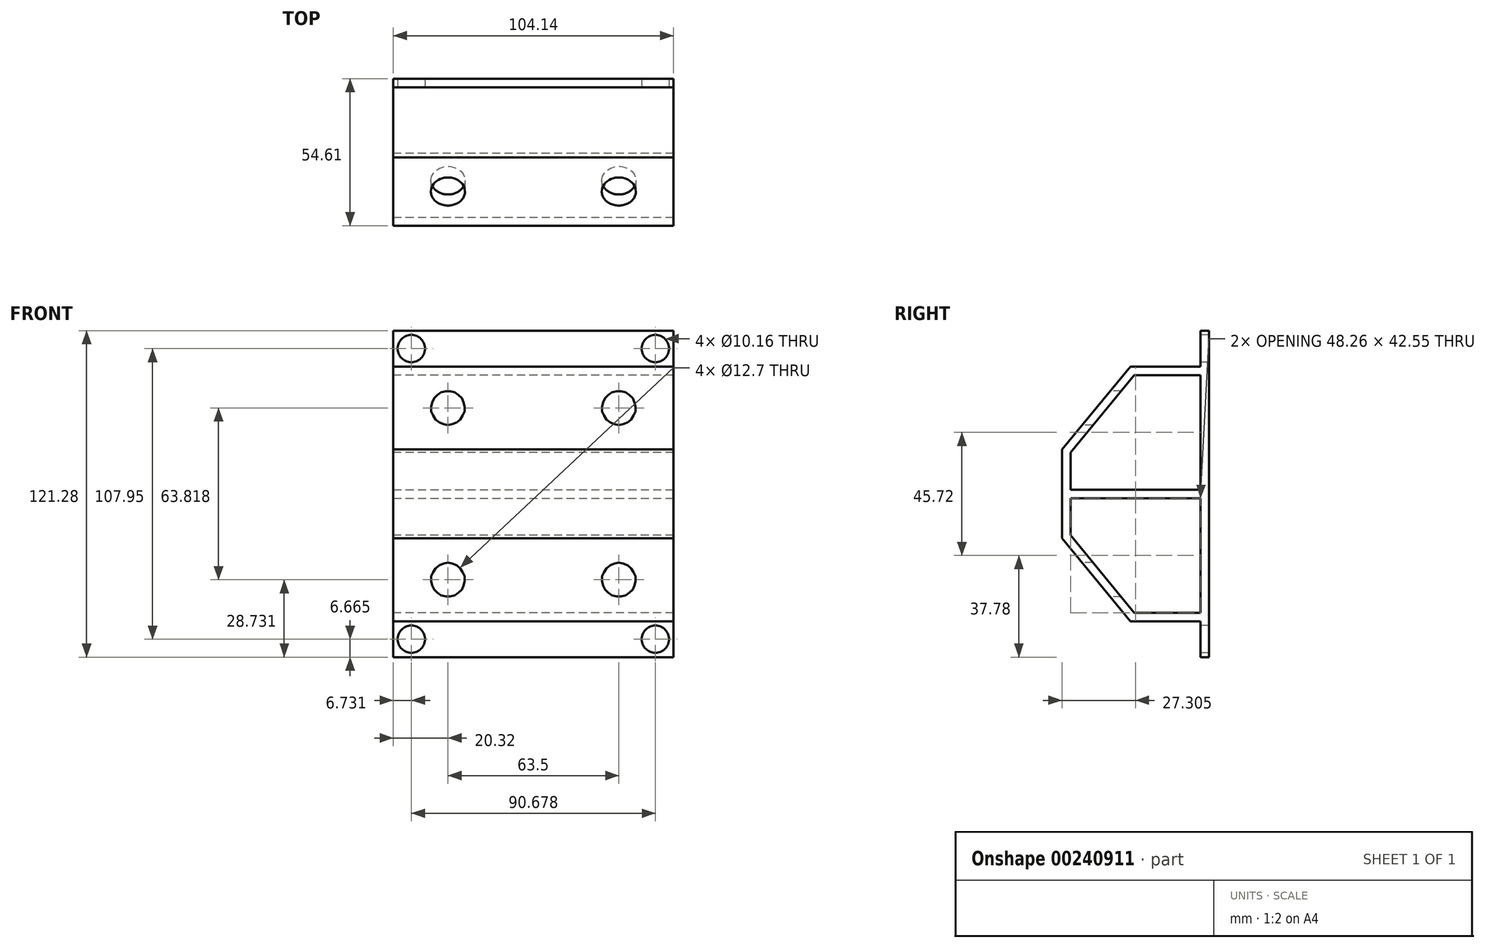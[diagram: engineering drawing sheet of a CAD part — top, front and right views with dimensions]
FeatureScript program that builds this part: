
annotation { "Feature Type Name" : "Feature", "Feature Type Description" : "" }
export const myFeature = defineFeature(function(context is Context, id is Id, definition is map)
    precondition{}
    {
        {
            var Q0;
            Q0=qCreatedBy(makeId("Right.planeOp"),FACE);
            var sketch = newSketch(context, id + "F0", { "sketchPlane" : qUnion([Q0])});
            skLineSegment(sketch, "E0", {"start": v(0, 0) * mm, "end": v(57.67, 0) * mm, "construction": true});
            skLineSegment(sketch, "E1", {"start": v(29.21, 47.3) * mm, "end": v(0, 47.3) * mm});
            skLineSegment(sketch, "E2", {"start": v(0, 47.3) * mm, "end": v(-25.4, 16.51) * mm});
            skLineSegment(sketch, "E3", {"start": v(-25.4, 16.51) * mm, "end": v(-25.4, 0) * mm});
            skLineSegment(sketch, "E4", {"start": v(0, 0) * mm, "end": v(0, 100.35) * mm, "construction": true});
            skLineSegment(sketch, "E5", {"start": v(29.21, 47.3) * mm, "end": v(29.21, 0) * mm});
            skLineSegment(sketch, "E6.MirrorCS", {"start": v(29.21, -47.3) * mm, "end": v(29.21, 0) * mm});
            skLineSegment(sketch, "E7.MirrorCS", {"start": v(0, -47.3) * mm, "end": v(-25.4, -16.51) * mm});
            skLineSegment(sketch, "E8.MirrorCS", {"start": v(-25.4, -16.51) * mm, "end": v(-25.4, 0) * mm});
            skLineSegment(sketch, "E9.MirrorCS", {"start": v(29.21, -47.3) * mm, "end": v(0, -47.3) * mm});
            skLineSegment(sketch, "E10", {"start": v(-22.22, 3.17) * mm, "end": v(26.04, 3.17) * mm});
            skLineSegment(sketch, "E11.MirrorCS", {"start": v(-22.22, -3.17) * mm, "end": v(26.04, -3.17) * mm});
            skLineSegment(sketch, "E12.0", {"start": v(26.04, 44.13) * mm, "end": v(1.5, 44.13) * mm});
            skLineSegment(sketch, "E12.1", {"start": v(26.03, 44.13) * mm, "end": v(26.04, 0) * mm});
            skLineSegment(sketch, "E12.2", {"start": v(1.5, 44.13) * mm, "end": v(-22.22, 15.37) * mm});
            skLineSegment(sketch, "E12.3", {"start": v(26.04, -44.13) * mm, "end": v(26.03, 0) * mm});
            skLineSegment(sketch, "E12.4", {"start": v(-22.22, 15.37) * mm, "end": v(-22.22, 0) * mm});
            skLineSegment(sketch, "E12.5", {"start": v(-22.22, -15.37) * mm, "end": v(-22.22, 0) * mm});
            skLineSegment(sketch, "E12.6", {"start": v(1.5, -44.13) * mm, "end": v(-22.23, -15.37) * mm});
            skLineSegment(sketch, "E12.7", {"start": v(26.04, -44.13) * mm, "end": v(1.5, -44.13) * mm});
            skPoint(sketch, "E13.orphan", {"position": v(-25.4, 3.17) * mm});
            skPoint(sketch, "E14.orphan", {"position": v(-25.4, -3.17) * mm});
            skPoint(sketch, "E15.orphan", {"position": v(29.21, 3.18) * mm});
            skPoint(sketch, "E16.orphan", {"position": v(29.21, -3.18) * mm});
            skLineSegment(sketch, "E17", {"start": v(-22.22, 3.17) * mm, "end": v(-22.22, -3.17) * mm});
            skLineSegment(sketch, "E18", {"start": v(26.04, 3.18) * mm, "end": v(26.04, -3.18) * mm});
            skSolve(sketch);
        }
        {
            var Q0;
            Q0=qSketchRegion(id+"F0",true);
            extrude(context, id + "F1", {"entities" : qUnion([Q0]), "depth" : 52.07 * mm, "hasSecondDirection" : true, "secondDirectionOppositeDirection" : true, "secondDirectionDepth" : 52.07 * mm});
        }
        {
            var Q0;
            Q0=makeQuery(id+"F1.opExtrude","CAP_FACE",FACE,{"disambiguationData":[OSD([sQuery(id+"F0.wireOp",EDGE,"E1"),sQuery(id+"F0.wireOp",EDGE,"E2"),sQuery(id+"F0.wireOp",EDGE,"E3"),sQuery(id+"F0.wireOp",EDGE,"E5"),sQuery(id+"F0.wireOp",EDGE,"E6.MirrorCS"),sQuery(id+"F0.wireOp",EDGE,"E7.MirrorCS"),sQuery(id+"F0.wireOp",EDGE,"E8.MirrorCS"),sQuery(id+"F0.wireOp",EDGE,"E9.MirrorCS"),sQuery(id+"F0.wireOp",EDGE,"E12.0"),sQuery(id+"F0.wireOp",EDGE,"E12.1"),sQuery(id+"F0.wireOp",EDGE,"E12.2"),sQuery(id+"F0.wireOp",EDGE,"E12.3"),sQuery(id+"F0.wireOp",EDGE,"E12.4"),sQuery(id+"F0.wireOp",EDGE,"E12.5"),sQuery(id+"F0.wireOp",EDGE,"E12.6"),sQuery(id+"F0.wireOp",EDGE,"E12.7"),sQuery(id+"F0.wireOp",EDGE,"E17"),sQuery(id+"F0.wireOp",EDGE,"E18")])],"isStart":false});
            var sketch = newSketch(context, id + "F2", { "sketchPlane" : qUnion([Q0])});
            skLineSegment(sketch, "E19", {"start": v(-22.22, 1.59) * mm, "end": v(26.04, 1.59) * mm});
            skLineSegment(sketch, "E20", {"start": v(0, 0) * mm, "end": v(9.33, 0) * mm, "construction": true});
            skLineSegment(sketch, "E21.MirrorCS", {"start": v(-22.22, -1.59) * mm, "end": v(26.04, -1.59) * mm});
            skLineSegment(sketch, "E22", {"start": v(-22.22, 1.59) * mm, "end": v(-22.22, -1.59) * mm});
            skLineSegment(sketch, "E23", {"start": v(26.04, 1.59) * mm, "end": v(26.04, -1.59) * mm});
            skSolve(sketch);
        }
        {
            var Q0;
            Q0=qSketchRegion(id+"F2",true);
            var Q1;
            Q1=makeQuery(id+"F1.opExtrude","CAP_FACE",FACE,{"disambiguationData":[OSD([sQuery(id+"F0.wireOp",EDGE,"E1"),sQuery(id+"F0.wireOp",EDGE,"E2"),sQuery(id+"F0.wireOp",EDGE,"E3"),sQuery(id+"F0.wireOp",EDGE,"E5"),sQuery(id+"F0.wireOp",EDGE,"E6.MirrorCS"),sQuery(id+"F0.wireOp",EDGE,"E7.MirrorCS"),sQuery(id+"F0.wireOp",EDGE,"E8.MirrorCS"),sQuery(id+"F0.wireOp",EDGE,"E9.MirrorCS"),sQuery(id+"F0.wireOp",EDGE,"E12.0"),sQuery(id+"F0.wireOp",EDGE,"E12.1"),sQuery(id+"F0.wireOp",EDGE,"E12.2"),sQuery(id+"F0.wireOp",EDGE,"E12.3"),sQuery(id+"F0.wireOp",EDGE,"E12.4"),sQuery(id+"F0.wireOp",EDGE,"E12.5"),sQuery(id+"F0.wireOp",EDGE,"E12.6"),sQuery(id+"F0.wireOp",EDGE,"E12.7"),sQuery(id+"F0.wireOp",EDGE,"E17"),sQuery(id+"F0.wireOp",EDGE,"E18")])],"isStart":true});
            extrude(context, id + "F3", {"entities" : qUnion([Q0]), "operationType" : NewBodyOperationType.ADD, "endBound" : BoundingType.UP_TO_SURFACE, "oppositeDirection" : true, "endBoundEntityFace" : qUnion([Q1]), "depth" : 25.4 * mm});
        }
        {
            var Q0;
            Q0=makeQuery(id+"F1.opExtrude","SWEPT_FACE",FACE,{"disambiguationData":[OSD([sQuery(id+"F0.wireOp",EDGE,"E5"),sQuery(id+"F0.wireOp",EDGE,"E6.MirrorCS")])]});
            var sketch = newSketch(context, id + "F4", { "sketchPlane" : qUnion([Q0])});
            skLineSegment(sketch, "E24", {"start": v(-52.07, 47.3) * mm, "end": v(-52.07, 60.64) * mm});
            skLineSegment(sketch, "E25", {"start": v(-52.07, 60.64) * mm, "end": v(52.07, 60.64) * mm});
            skLineSegment(sketch, "E26", {"start": v(52.07, 60.64) * mm, "end": v(52.07, 47.3) * mm});
            skLineSegment(sketch, "E27", {"start": v(52.07, 47.3) * mm, "end": v(-52.07, 47.3) * mm});
            skLineSegment(sketch, "E28", {"start": v(0, 0) * mm, "end": v(26.61, 0) * mm, "construction": true});
            skLineSegment(sketch, "E29.MirrorCS", {"start": v(52.07, -47.3) * mm, "end": v(-52.07, -47.3) * mm});
            skLineSegment(sketch, "E30.MirrorCS", {"start": v(52.07, -60.64) * mm, "end": v(52.07, -47.3) * mm});
            skLineSegment(sketch, "E31.MirrorCS", {"start": v(-52.07, -60.64) * mm, "end": v(52.07, -60.64) * mm});
            skLineSegment(sketch, "E32.MirrorCS", {"start": v(-52.07, -47.3) * mm, "end": v(-52.07, -60.64) * mm});
            skSolve(sketch);
        }
        {
            var Q0;
            Q0=qSketchRegion(id+"F4",true);
            extrude(context, id + "F5", {"entities" : qUnion([Q0]), "operationType" : NewBodyOperationType.ADD, "oppositeDirection" : true, "depth" : 3.17 * mm});
        }
        {
            var Q0;
            Q0=makeQuery(id+"F5.opExtrude","CAP_FACE",FACE,{"disambiguationData":[OSD([sQuery(id+"F4.wireOp",EDGE,"E24"),sQuery(id+"F4.wireOp",EDGE,"E25"),sQuery(id+"F4.wireOp",EDGE,"E26"),sQuery(id+"F4.wireOp",EDGE,"E27")])],"isStart":false});
            var sketch = newSketch(context, id + "F6", { "sketchPlane" : qUnion([Q0])});
            skCircle(sketch, "E33", {"center": v(-45.34, 53.97) * mm, "radius": 5.08 * mm});
            skPoint(sketch, "E33.centerSnap0", {"position": v(-52.07, 53.97) * mm});
            skCircle(sketch, "E34", {"center": v(45.34, 53.97) * mm, "radius": 5.08 * mm});
            skLineSegment(sketch, "E35", {"start": v(0, 0) * mm, "end": v(81.74, 0) * mm, "construction": true});
            skCircle(sketch, "E36.MirrorC", {"center": v(45.34, -53.97) * mm, "radius": 5.08 * mm});
            skCircle(sketch, "E37.MirrorC", {"center": v(-45.34, -53.98) * mm, "radius": 5.08 * mm});
            skSolve(sketch);
        }
        {
            var Q0;
            Q0=qSketchRegion(id+"F6",true);
            var Q1;
            Q1=makeQuery(id+"F5.boolean.opBoolean","MERGE",FACE,{"derivedFrom":[makeQuery(id+"F1.opExtrude","SWEPT_FACE",FACE,{"disambiguationData":[OSD([sQuery(id+"F0.wireOp",EDGE,"E5"),sQuery(id+"F0.wireOp",EDGE,"E6.MirrorCS")])]}),makeQuery(id+"F5.opExtrude","CAP_FACE",FACE,{"disambiguationData":[OSD([sQuery(id+"F4.wireOp",EDGE,"E24"),sQuery(id+"F4.wireOp",EDGE,"E25"),sQuery(id+"F4.wireOp",EDGE,"E26"),sQuery(id+"F4.wireOp",EDGE,"E27")])],"isStart":true}),makeQuery(id+"F5.opExtrude","CAP_FACE",FACE,{"disambiguationData":[OSD([sQuery(id+"F4.wireOp",EDGE,"E29.MirrorCS"),sQuery(id+"F4.wireOp",EDGE,"E30.MirrorCS"),sQuery(id+"F4.wireOp",EDGE,"E31.MirrorCS"),sQuery(id+"F4.wireOp",EDGE,"E32.MirrorCS")])],"isStart":true})]});
            extrude(context, id + "F7", {"entities" : qUnion([Q0]), "operationType" : NewBodyOperationType.REMOVE, "endBound" : BoundingType.UP_TO_SURFACE, "oppositeDirection" : true, "endBoundEntityFace" : qUnion([Q1]), "depth" : 25.4 * mm});
        }
        {
            var Q0;
            Q0=makeQuery(id+"F1.opExtrude","SWEPT_FACE",FACE,{"disambiguationData":[OSD([sQuery(id+"F0.wireOp",EDGE,"E3"),sQuery(id+"F0.wireOp",EDGE,"E8.MirrorCS")])]});
            var sketch = newSketch(context, id + "F8", { "sketchPlane" : qUnion([Q0])});
            skCircle(sketch, "E38", {"center": v(-31.75, 31.9) * mm, "radius": 6.35 * mm});
            skLineSegment(sketch, "E39", {"start": v(0, 0) * mm, "end": v(0, 55.11) * mm, "construction": true});
            skLineSegment(sketch, "E40", {"start": v(0, 0) * mm, "end": v(34.58, 0) * mm, "construction": true});
            skLineSegment(sketch, "E41", {"start": v(52.07, 47.3) * mm, "end": v(52.07, 16.5) * mm, "construction": true});
            skLineSegment(sketch, "E42", {"start": v(52.07, 31.9) * mm, "end": v(-54.5, 31.9) * mm, "construction": true});
            skCircle(sketch, "E43.MirrorC", {"center": v(31.75, 31.9) * mm, "radius": 6.35 * mm});
            skCircle(sketch, "E44.MirrorC", {"center": v(31.75, -31.9) * mm, "radius": 6.35 * mm});
            skCircle(sketch, "E45.MirrorC", {"center": v(-31.75, -31.9) * mm, "radius": 6.35 * mm});
            skSolve(sketch);
        }
        {
            var Q0;
            Q0=qSketchRegion(id+"F8",true);
            var Q1;
            {var subQ0=sQuery(id+"F0.wireOp",EDGE,"E18");var subQ6=sQuery(id+"F0.wireOp",EDGE,"E12.3");var subQ8=sQuery(id+"F0.wireOp",EDGE,"E12.1");var subQ9=sQuery(id+"F0.wireOp",EDGE,"E12.0");Q1=makeQuery(id+"F3.boolean.opBoolean","SPLIT",FACE,{"disambiguationData":[TD([makeQuery(id+"F1.opExtrude","SWEPT_FACE",FACE,{"disambiguationData":[OSD([subQ9])]})])],"derivedFrom":makeQuery(id+"F1.opExtrude","SWEPT_FACE",FACE,{"disambiguationData":[OSD([subQ8,subQ6,subQ0])]})});}
            extrude(context, id + "F9", {"entities" : qUnion([Q0]), "operationType" : NewBodyOperationType.REMOVE, "endBound" : BoundingType.UP_TO_SURFACE, "oppositeDirection" : true, "endBoundEntityFace" : qUnion([Q1]), "depth" : 25.4 * mm});
        }
    });
